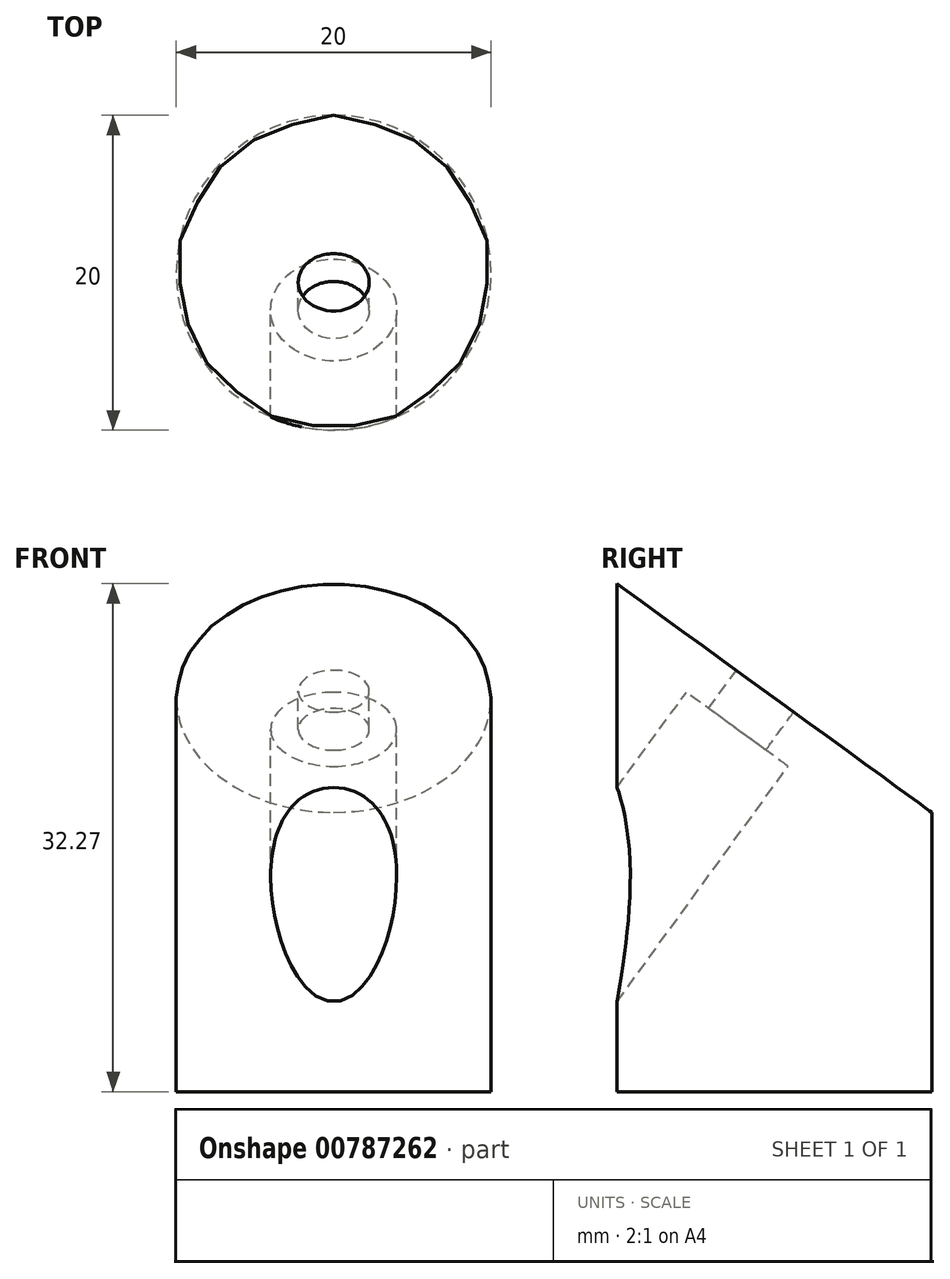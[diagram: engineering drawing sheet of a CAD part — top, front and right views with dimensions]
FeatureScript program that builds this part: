
annotation { "Feature Type Name" : "Feature", "Feature Type Description" : "" }
export const myFeature = defineFeature(function(context is Context, id is Id, definition is map)
    precondition{}
    {
        {
            var Q0;
            Q0=qCreatedBy(makeId("Right.planeOp"),FACE);
            var sketch = newSketch(context, id + "F0", { "sketchPlane" : qUnion([Q0])});
            skLineSegment(sketch, "E0", {"start": v(-42.65, 30.99) * mm, "end": v(0, 0) * mm, "construction": true});
            skLineSegment(sketch, "E1", {"start": v(0, 0) * mm, "end": v(36.16, -26.27) * mm, "construction": true});
            skSolve(sketch);
        }
        {
            var Q0;
            Q0=sQuery(id+"F0.wireOp",EDGE,"E0");
            var Q1;
            Q1=qCreatedBy(makeId("Top.planeOp"),FACE);
            cPlane(context, id + "F1", {"entities" : qUnion([Q0, Q1]), "cplaneType" : CPlaneType.LINE_ANGLE, "offset" : 25 * mm, "angle" : 0 * degree, "width" : 150 * mm, "height" : 150 * mm});
        }
        {
            var Q0;
            Q0=qCreatedBy(makeId("Top.planeOp"),FACE);
            var sketch = newSketch(context, id + "F2", { "sketchPlane" : qUnion([Q0])});
            skCircle(sketch, "E2", {"center": v(0, 0) * mm, "radius": 4 * mm, "construction": true});
            skCircle(sketch, "E3", {"center": v(0, 0) * mm, "radius": 10 * mm});
            skSolve(sketch);
        }
        {
            var Q0;
            Q0=makeQuery(id+"F2.imprint","IMPRINT",FACE,{"disambiguationData":[TD([[makeQuery(id+"F2.imprint","IMPRINT",EDGE,{"derivedFrom":sQuery(id+"F2.wireOp",EDGE,"E3")}),1.0]])]});
            var Q1;
            Q1=qCreatedBy(id+"F1.planeOp",FACE);
            extrude(context, id + "F3", {"entities" : qUnion([Q0]), "endBound" : BoundingType.UP_TO_SURFACE, "depth" : 25 * mm, "endBoundEntityFace" : qUnion([Q1]), "offsetDistance" : 25 * mm, "hasSecondDirection" : true, "secondDirectionOppositeDirection" : true, "secondDirectionDepth" : 25 * mm});
        }
        {
            var Q0;
            Q0=qCreatedBy(id+"F1.planeOp",FACE);
            var sketch = newSketch(context, id + "F4", { "sketchPlane" : qUnion([Q0])});
            skCircle(sketch, "E4", {"center": v(0, 0.75) * mm, "radius": 4 * mm});
            skCircle(sketch, "E5", {"center": v(0, 0.75) * mm, "radius": 2.25 * mm});
            skSolve(sketch);
        }
        {
            var Q0;
            Q0=makeQuery(id+"F4.imprint","IMPRINT",FACE,{"disambiguationData":[TD([[makeQuery(id+"F4.imprint","IMPRINT",EDGE,{"derivedFrom":sQuery(id+"F4.wireOp",EDGE,"E4")}),1.0]])]});
            var Q1;
            Q1=makeQuery(id+"F4.imprint","IMPRINT",FACE,{"disambiguationData":[TD([[makeQuery(id+"F4.imprint","IMPRINT",EDGE,{"derivedFrom":sQuery(id+"F4.wireOp",EDGE,"E5")}),1.0]])]});
            extrude(context, id + "F5", {"entities" : qUnion([Q0, Q1]), "operationType" : NewBodyOperationType.REMOVE, "depth" : 25 * mm, "offsetDistance" : 25 * mm, "hasSecondDirection" : true, "secondDirectionOppositeDirection" : false, "secondDirectionDepth" : 3 * mm});
        }
        {
            var Q0;
            Q0=makeQuery(id+"F4.imprint","IMPRINT",FACE,{"disambiguationData":[TD([[makeQuery(id+"F4.imprint","IMPRINT",EDGE,{"derivedFrom":sQuery(id+"F4.wireOp",EDGE,"E5")}),1.0]])]});
            extrude(context, id + "F6", {"entities" : qUnion([Q0]), "operationType" : NewBodyOperationType.REMOVE, "depth" : 25 * mm, "offsetDistance" : 25 * mm});
        }
    });
